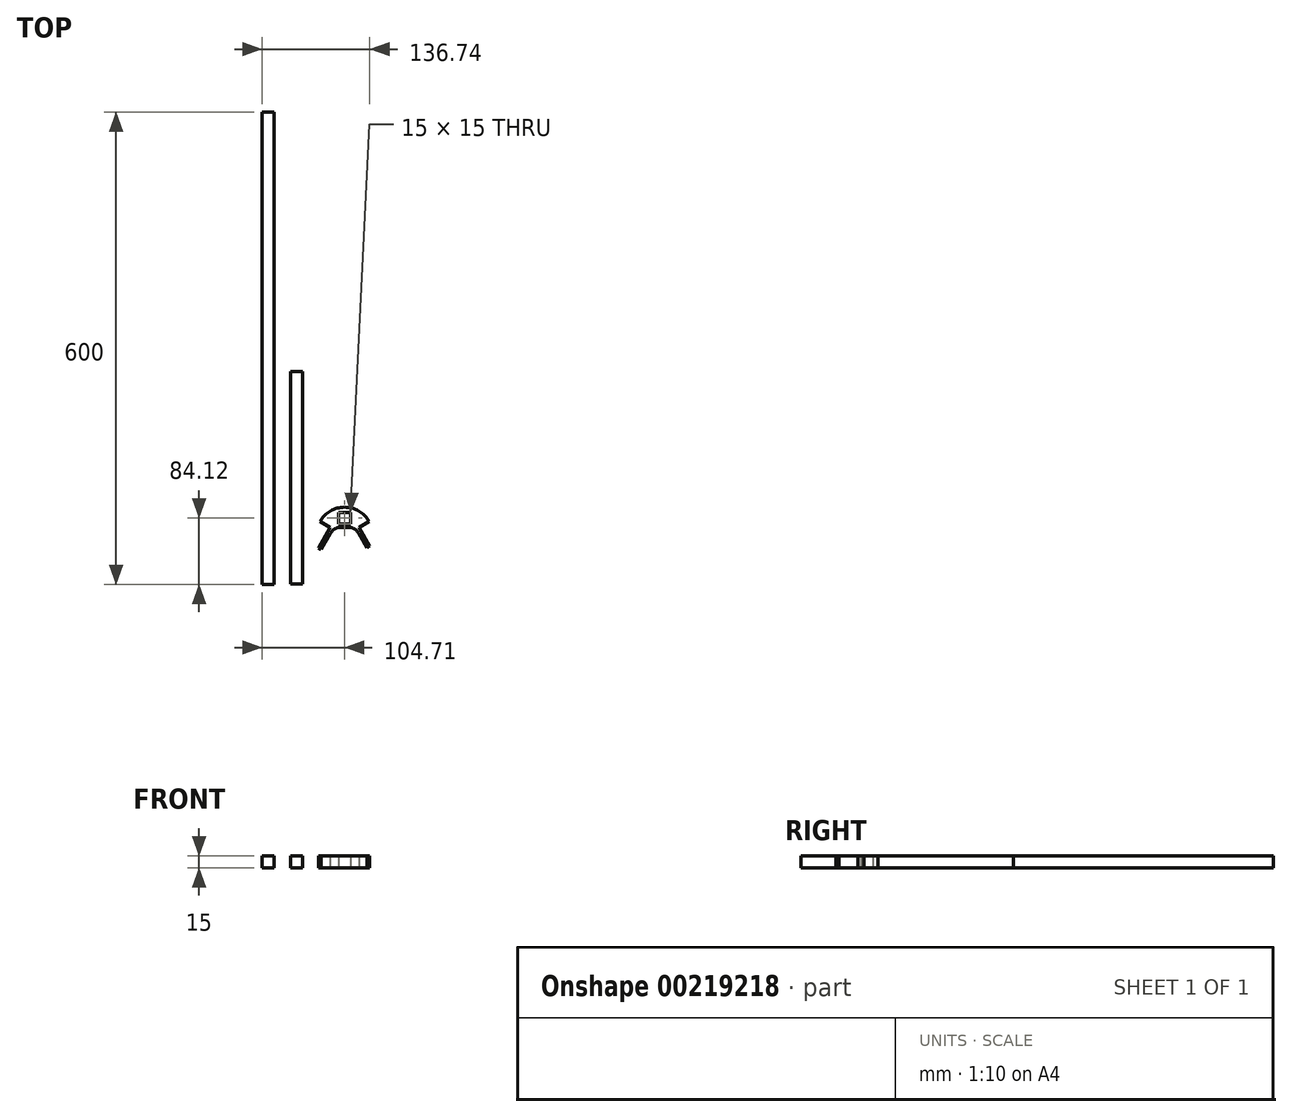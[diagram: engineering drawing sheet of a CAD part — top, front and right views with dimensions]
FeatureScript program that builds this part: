
annotation { "Feature Type Name" : "Feature", "Feature Type Description" : "" }
export const myFeature = defineFeature(function(context is Context, id is Id, definition is map)
    precondition{}
    {
        {
            assignVariable(context, id + "F0", {"name" : "extrusion_side", "anyValue" : 15 * mm});
        }
        {
            var Q0;
            Q0=qCreatedBy(makeId("Top.planeOp"),FACE);
            var sketch = newSketch(context, id + "F1", { "sketchPlane" : qUnion([Q0])});
            skLineSegment(sketch, "E0", {"start": v(-31.18, -4) * mm, "end": v(-18.19, -11.5) * mm});
            skLineSegment(sketch, "E1", {"start": v(18.19, -11.5) * mm, "end": v(31.18, -4) * mm});
            skLineSegment(sketch, "E2.bottom", {"start": v(7.5, 7.5) * mm, "end": v(-7.5, 7.5) * mm});
            skLineSegment(sketch, "E2.top", {"start": v(7.5, -7.5) * mm, "end": v(-7.5, -7.5) * mm});
            skLineSegment(sketch, "E2.left", {"start": v(7.5, 7.5) * mm, "end": v(7.5, -7.5) * mm});
            skLineSegment(sketch, "E2.right", {"start": v(-7.5, 7.5) * mm, "end": v(-7.5, -7.5) * mm});
            skPoint(sketch, "E2.middle", {"position": v(0, 0) * mm});
            skArc(sketch, "E3", {"start": v(31.18, -4) * mm, "mid": v(0, 14) * mm, "end": v(-31.18, -4) * mm});
            skLineSegment(sketch, "E4", {"start": v(-18.19, -11.5) * mm, "end": v(-33.19, -37.48) * mm});
            skLineSegment(sketch, "E5", {"start": v(-33.19, -37.48) * mm, "end": v(-29.72, -39.48) * mm});
            skLineSegment(sketch, "E6", {"start": v(-29.72, -39.48) * mm, "end": v(-13.57, -11.5) * mm});
            skLineSegment(sketch, "E7", {"start": v(-13.57, -11.5) * mm, "end": v(13.57, -11.5) * mm});
            skLineSegment(sketch, "E8", {"start": v(13.57, -11.5) * mm, "end": v(28.57, -37.48) * mm});
            skLineSegment(sketch, "E9", {"start": v(28.57, -37.48) * mm, "end": v(32.03, -35.48) * mm});
            skLineSegment(sketch, "E10", {"start": v(32.03, -35.48) * mm, "end": v(18.19, -11.5) * mm});
            skLineSegment(sketch, "E11", {"start": v(-31.18, -4) * mm, "end": v(-39.2, -17.9) * mm, "construction": true});
            skSolve(sketch);
        }
        {
            var Q0;
            Q0=makeQuery(id+"F1.imprint","IMPRINT",FACE,{"disambiguationData":[TD([[makeQuery(id+"F1.imprint","IMPRINT",EDGE,{"derivedFrom":sQuery(id+"F1.wireOp",EDGE,"E0")}),1.0]])]});
            extrude(context, id + "F2", {"entities" : qUnion([Q0]), "depth" : getVariable(context, 'extrusion_side')});
        }
        {
            var Q0;
            Q0=makeQuery(id+"F2.opExtrude","SWEPT_EDGE",EDGE,{"disambiguationData":[OSD([sQuery(id+"F1.wireOp",EDGE,"E7"),sQuery(id+"F1.wireOp",EDGE,"E8")])]});
            var Q1;
            Q1=makeQuery(id+"F2.opExtrude","SWEPT_EDGE",EDGE,{"disambiguationData":[OSD([sQuery(id+"F1.wireOp",EDGE,"E6"),sQuery(id+"F1.wireOp",EDGE,"E7")])]});
            fillet(context, id + "F3", {"entities" : qUnion([Q0, Q1]), "radius" : getVariable(context, 'extrusion_side'), "tangentPropagation" : true, "allowEdgeOverflow" : false});
        }
        {
            var Q0;
            Q0=qCreatedBy(makeId("Top.planeOp"),FACE);
            var sketch = newSketch(context, id + "F4", { "sketchPlane" : qUnion([Q0])});
            skLineSegment(sketch, "E12.bottom", {"start": v(-68.58, 186.18) * mm, "end": v(-53.58, 186.18) * mm});
            skLineSegment(sketch, "E12.top", {"start": v(-68.58, -83.82) * mm, "end": v(-53.58, -83.82) * mm});
            skLineSegment(sketch, "E12.left", {"start": v(-68.58, 186.18) * mm, "end": v(-68.58, -83.82) * mm});
            skLineSegment(sketch, "E12.right", {"start": v(-53.58, 186.18) * mm, "end": v(-53.58, -83.82) * mm});
            skLineSegment(sketch, "E13.bottom", {"start": v(-89.7, -84.12) * mm, "end": v(-104.7, -84.12) * mm});
            skLineSegment(sketch, "E13.top", {"start": v(-89.7, 515.88) * mm, "end": v(-104.7, 515.88) * mm});
            skLineSegment(sketch, "E13.left", {"start": v(-89.7, -84.12) * mm, "end": v(-89.7, 515.88) * mm});
            skLineSegment(sketch, "E13.right", {"start": v(-104.7, -84.12) * mm, "end": v(-104.7, 515.88) * mm});
            skSolve(sketch);
        }
        {
            var Q0;
            Q0=makeQuery(id+"F4.imprint","IMPRINT",FACE,{"disambiguationData":[TD([[makeQuery(id+"F4.imprint","IMPRINT",EDGE,{"derivedFrom":sQuery(id+"F4.wireOp",EDGE,"E12.bottom")}),-1.0]])]});
            extrude(context, id + "F5", {"entities" : qUnion([Q0]), "depth" : getVariable(context, 'extrusion_side')});
        }
        {
            var Q0;
            Q0=makeQuery(id+"F4.imprint","IMPRINT",FACE,{"disambiguationData":[TD([[makeQuery(id+"F4.imprint","IMPRINT",EDGE,{"derivedFrom":sQuery(id+"F4.wireOp",EDGE,"E13.bottom")}),-1.0]])]});
            extrude(context, id + "F6", {"entities" : qUnion([Q0]), "depth" : getVariable(context, 'extrusion_side')});
        }
    });
